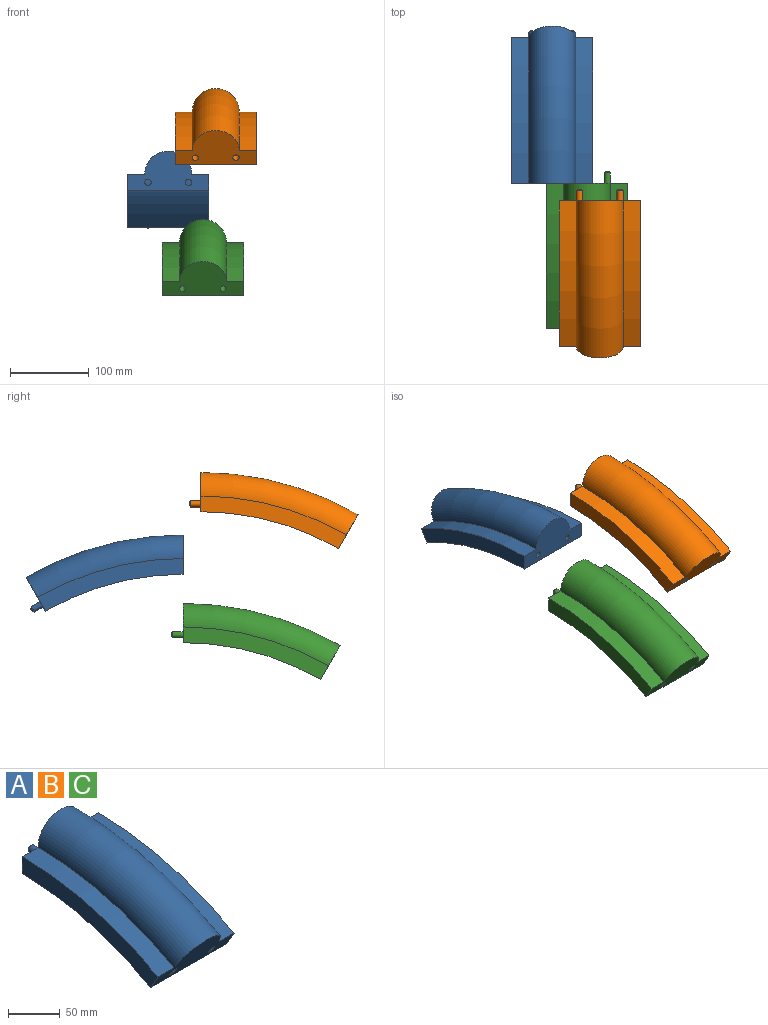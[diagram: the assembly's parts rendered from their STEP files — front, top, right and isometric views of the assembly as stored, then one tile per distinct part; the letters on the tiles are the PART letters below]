
ASSEMBLY  parts=3 mates=1
PART A: 18 faces, bbox 103.6x231.4x129.7 mm
  f0: cylinder r=350mm len=175mm, axis (-1,0,0), area 18984.4mm2, adj f1,f5,f6,f7
  f1: plane 185x66.89mm, normal (1,0,0), area 3769.9mm2, adj f0,f2,f6,f7
  f2: cylinder r=370mm len=185mm, axis (-1,0,0), area 4240.9mm2, adj f1,f3,f6,f7
  f3: torus R=370mm, axis (-1,0,0), area 19138mm2, adj f2,f4,f6,f7
  f4: cylinder r=370mm len=185mm, axis (-1,0,0), area 4240.9mm2, adj f3,f5,f6,f7
  f5: plane 185x66.89mm, normal (-1,0,0), area 3769.9mm2, adj f0,f4,f6,f7
  f6: plane 103.59x43.22mm, normal (0,-0.87,-0.5), area 3373.6mm2, adj f0,f1,f2,f3,f4,f5,f14,f16
  f7: plane 103.59x49.91mm, normal (0,1,0), area 3376.2mm2, adj f0,f1,f2,f3,f4,f5,f8,f10
  f8: cylinder r=4mm len=13mm, axis (0,-1,0), area 326.7mm2, adj f7,f12
  f9: plane 4x4mm, normal (0,1,0), area 12.6mm2, adj f12
  f10: cylinder r=4mm len=13mm, axis (0,-1,0), area 326.7mm2, adj f7,f13
  f11: plane 4x4mm, normal (0,1,0), area 12.6mm2, adj f13
  f12: cone r=2mm half-angle=45deg, axis (0,-1,0), area 53.3mm2, adj f8,f9
  f13: cone r=2mm half-angle=45deg, axis (0,-1,0), area 53.3mm2, adj f10,f11
  f14: cylinder r=4.05mm len=17.91mm, axis (0,-0.87,-0.5), area 407.2mm2, adj f6,f15
  f15: plane 8.1x7.02mm, normal (0,-0.87,-0.5), area 51.5mm2, adj f14
  f16: cylinder r=4.05mm len=17.91mm, axis (0,-0.87,-0.5), area 407.2mm2, adj f6,f17
  f17: plane 8.1x7.02mm, normal (0,-0.87,-0.5), area 51.5mm2, adj f16
PART B: same geometry as A
PART C: same geometry as A
PLACE A rot(axis=(-1,0,0),30deg) t=(-310.53,108.43,-224.85)mm
PLACE B t=(-250.08,85.59,-145.26)mm
PLACE C t=(-266.31,108.43,-311.98)mm
MATE planar A.f6 <-> C.f7  axis (0,-1,0) through (-310.53,108.43,145.15)mm
